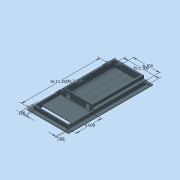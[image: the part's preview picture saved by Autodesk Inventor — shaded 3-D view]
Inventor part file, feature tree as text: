
AUTODESK INVENTOR PART (.ipt)
format: ipt  version: 2015 (Build 190159000, 159)  size: 186,368 bytes
history: native  units: in
note: dims shown in document units (in); Inventor stores cm internally (conversion verified against a paired STEP export)
features: extrude x8, sketch x5, plane x1, projected_geometry x1
ambient origin geometry x8: Origin, YZ Plane, XZ Plane, XY Plane, X Axis, Y Axis, Z Axis, Center Point
bodies: Solid1 (feature_tree)
feature tree (15):
  sketch  "Sketch1"  dims[d0=5.5in d1=12.2647in]
  extrude  "Extrusion1"  Depth=12.2647in
  extrude  "Extrusion2"  Depth=0.1875in
  extrude  "Extrusion3"  Depth=4.0in
  extrude  "Extrusion4"  Depth=0.25in
  extrude  "Extrusion5"  Depth=0.25in
  extrude  "Extrusion6"  Depth=0.25in
  extrude  "Extrusion8"  Depth=1.1486in
  extrude  "Extrusion7"  TaperAngle=0.0deg  [1 undecoded]
  plane  "Work Plane1"
  sketch  "Sketch2"  dims[d2=0.1875in d3=0.1875in]
  sketch  "Sketch3"  dims[d4=0.1875in d5=4.0in]
  sketch  "Sketch4"  dims[d6=4.1045in d7=0.25in]
  projected_geometry  "Projected Loop1"
  sketch  "Sketch5"  dims[d8=7.7022in d9=0.25in d10=0.25in d11=1.1486in d12=0.0in d13=0.1875in d14=0.0in d15=0.125in d16=0.0in d17=0.6875in d18=0.0in d19=1.0236in d20=1.0236in d21=1.0236in d22=1.0236in d23=0.6875in d24=0.0in d25=0.625in d26=0.625in d27=0.6875in d28=0.0in d29=1.0in d30=0.6875in d31=0.0in d32=0.5in d33=0.5in d34=0.5in d35=0.5in d36=0.125in d37=0.0in]
note: 1 required parameter value undecoded (feature->parameter linkage not recoverable at this tier; creation-order binding heuristic only, values carry confidence <= 0.55)
